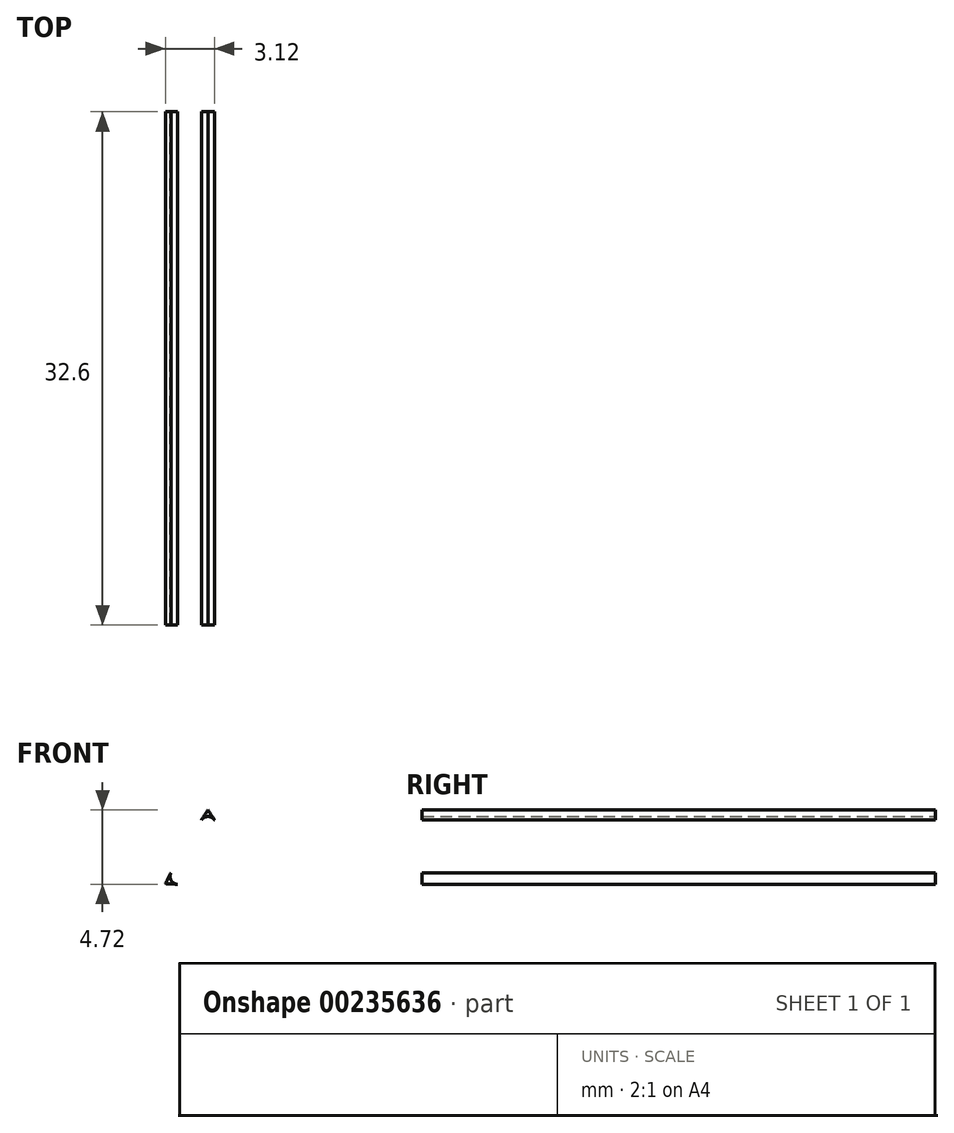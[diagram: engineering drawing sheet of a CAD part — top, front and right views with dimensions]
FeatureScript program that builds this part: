
annotation { "Feature Type Name" : "Feature", "Feature Type Description" : "" }
export const myFeature = defineFeature(function(context is Context, id is Id, definition is map)
    precondition{}
    {
        {
            var Q0;
            Q0=qCreatedBy(makeId("Front.planeOp"),FACE);
            var sketch = newSketch(context, id + "F0", { "sketchPlane" : qUnion([Q0])});
            skFitSpline(sketch, "E0", {"points": [v(0, 0) * mm, v(1.26, 2.39) * mm, v(2.7, 4.68) * mm], "startDerivative": vector(2.44, 4.83) * mm, "endDerivative": vector(2.96, 4.53) * mm});
            skFitSpline(sketch, "E1", {"points": [v(2.7, 4.68) * mm, v(4.14, 2.39) * mm, v(5.4, 0) * mm], "startDerivative": vector(2.96, -4.53) * mm, "endDerivative": vector(2.44, -4.83) * mm});
            skFitSpline(sketch, "E2", {"points": [v(5.4, 0) * mm, v(2.7, -0.1) * mm, v(0, 0) * mm], "startDerivative": vector(-5.4, -0.3) * mm, "endDerivative": vector(-5.4, 0.3) * mm});
            skArc(sketch, "E3.filletArc", {"start": v(3.12, 4.03) * mm, "mid": v(2.7, 4.26) * mm, "end": v(2.28, 4.03) * mm});
            skArc(sketch, "E4.filletArc", {"start": v(4.63, -0.04) * mm, "mid": v(5.04, 0.2) * mm, "end": v(5.05, 0.69) * mm});
            skArc(sketch, "E5.filletArc", {"start": v(0.35, 0.69) * mm, "mid": v(0.36, 0.2) * mm, "end": v(0.77, -0.04) * mm});
            skSolve(sketch);
        }
        {
            var Q0;
            Q0=makeQuery(id+"F0.imprint","IMPRINT",FACE,{"disambiguationData":[TD([[makeQuery(id+"F0.imprint","IMPRINT",EDGE,{"derivedFrom":sQuery(id+"F0.wireOp",EDGE,"E0")}),-1.0]])]});
            extrude(context, id + "F1", {"entities" : qUnion([Q0]), "depth" : 32.6 * mm});
        }
    });
